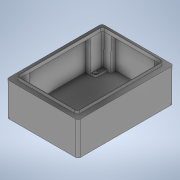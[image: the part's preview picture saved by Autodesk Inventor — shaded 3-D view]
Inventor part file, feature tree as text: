
AUTODESK INVENTOR PART (.ipt)
format: ipt  version: 2021 (Build 250183000, 183)  size: 472,064 bytes
history: native  units: mm
features: extrude x13, sketch x11, projected_geometry x10, draft x7, plane x6, shell x1, fillet x1, hole x1
ambient origin geometry x8: Origin, YZ Plane, XZ Plane, XY Plane, X Axis, Y Axis, Z Axis, Center Point
bodies: Solid1 (feature_tree)
feature tree (50):
  extrude  "Extrusion1"  Depth=398.5mm
  extrude  "Extrusion2"  Depth=139.8mm
  shell  "Shell1"  Thickness=256.0mm
  extrude  "Extrusion3"  Depth=10.0mm
  plane  "Work Plane1"
  plane  "Work Plane2"
  plane  "Work Plane3"
  plane  "Work Plane4"
  plane  "Work Plane5"
  plane  "Work Plane6"
  sketch  "Sketch4"  dims[d8=11.8mm d9=0.0mm d10=2.7mm]
  extrude  "Extrusion4"  Depth=2.7mm
  extrude  "Extrusion5"  Depth=17.0mm TaperAngle=0.0deg
  sketch  "Sketch5"  dims[d11=2.4mm d12=17.0mm d13=0.0mm]
  extrude  "Extrusion6"  Depth=247.0mm
  extrude  "Extrusion7"  Depth=14.0mm TaperAngle=0.0deg
  extrude  "Extrusion8"  Depth=14.0mm TaperAngle=0.0deg
  extrude  "Extrusion9"  Depth=351.5mm
  draft  "FaceDraft1"
  draft  "FaceDraft2"
  draft  "FaceDraft3"
  draft  "FaceDraft4"
  draft  "FaceDraft5"
  draft  "FaceDraft6"
  draft  "FaceDraft7"
  fillet  "Fillet1"  Radius=14.0mm
  extrude  "Extrusion10"  Depth=14.0mm
  extrude  "Extrusion11"  Depth=6.0mm
  extrude  "Extrusion12"  Depth=6.0mm
  extrude  "Extrusion13"  Depth=6.0mm
  hole  "Hole4"  [1 undecoded]
  sketch  "Sketch1"  dims[d0=298.5mm d1=398.5mm]
  sketch  "Sketch2"  dims[d2=10.0mm d3=139.8mm d4=0.053646mm d5=256.0mm]
  sketch  "Sketch3"  dims[d6=361.5mm d7=10.0mm]
  projected_geometry  "Projected Loop1"
  sketch  "Sketch6"  dims[d14=126.8mm d15=-126.8mm d16=89.5mm d17=-89.5mm d18=247.0mm]
  projected_geometry  "Projected Loop2"
  projected_geometry  "Projected Loop3"
  sketch  "Sketch7"  dims[d19=14.0mm d20=0.0mm d21=14.0mm d22=0.0mm]
  projected_geometry  "Projected Loop4"
  projected_geometry  "Projected Loop5"
  sketch  "Sketch8"  dims[d23=247.0mm d24=14.0mm d25=0.0mm]
  projected_geometry  "Projected Loop6"
  sketch  "Sketch9"  dims[d26=14.0mm d27=0.0mm d28=351.5mm d29=14.0mm d30=0.0mm]
  projected_geometry  "Projected Loop7"
  projected_geometry  "Projected Loop8"
  projected_geometry  "Projected Loop9"
  projected_geometry  "Projected Loop10"
  sketch  "Sketch11"  dims[d31=14.0mm d32=0.0mm d33=0.174533mm]
  sketch  "Sketch20"  dims[d34=0.174533mm d35=0.174533mm d36=0.174533mm d37=0.174533mm d38=0.174533mm d39=0.174533mm d40=6.0mm d41=20.0mm d43=12.0mm d44=8.2mm d45=0.0mm d46=15.82mm d47=15.82mm d48=15.82mm d49=15.82mm d50=228.7mm d51=228.7mm d52=275.7mm d53=275.7mm d54=114.35mm d55=114.35mm d56=137.85mm d57=137.85mm d58=8.0mm d59=0.0mm d60=7.9mm d61=7.9mm d62=7.9mm d63=7.9mm d64=7.9mm d65=0.0mm d66=245.0mm d67=289.0mm d68=211.0mm d69=259.0mm d70=2.0mm d71=0.0mm d154=213.0mm d155=335.0mm d156=3.0mm d157=8.0mm d158=4.0mm d159=2.0mm d160=90.0deg d161=6.0mm d162=20.594885mm]
note: 1 required parameter value undecoded (feature->parameter linkage not recoverable at this tier; creation-order binding heuristic only, values carry confidence <= 0.55)
